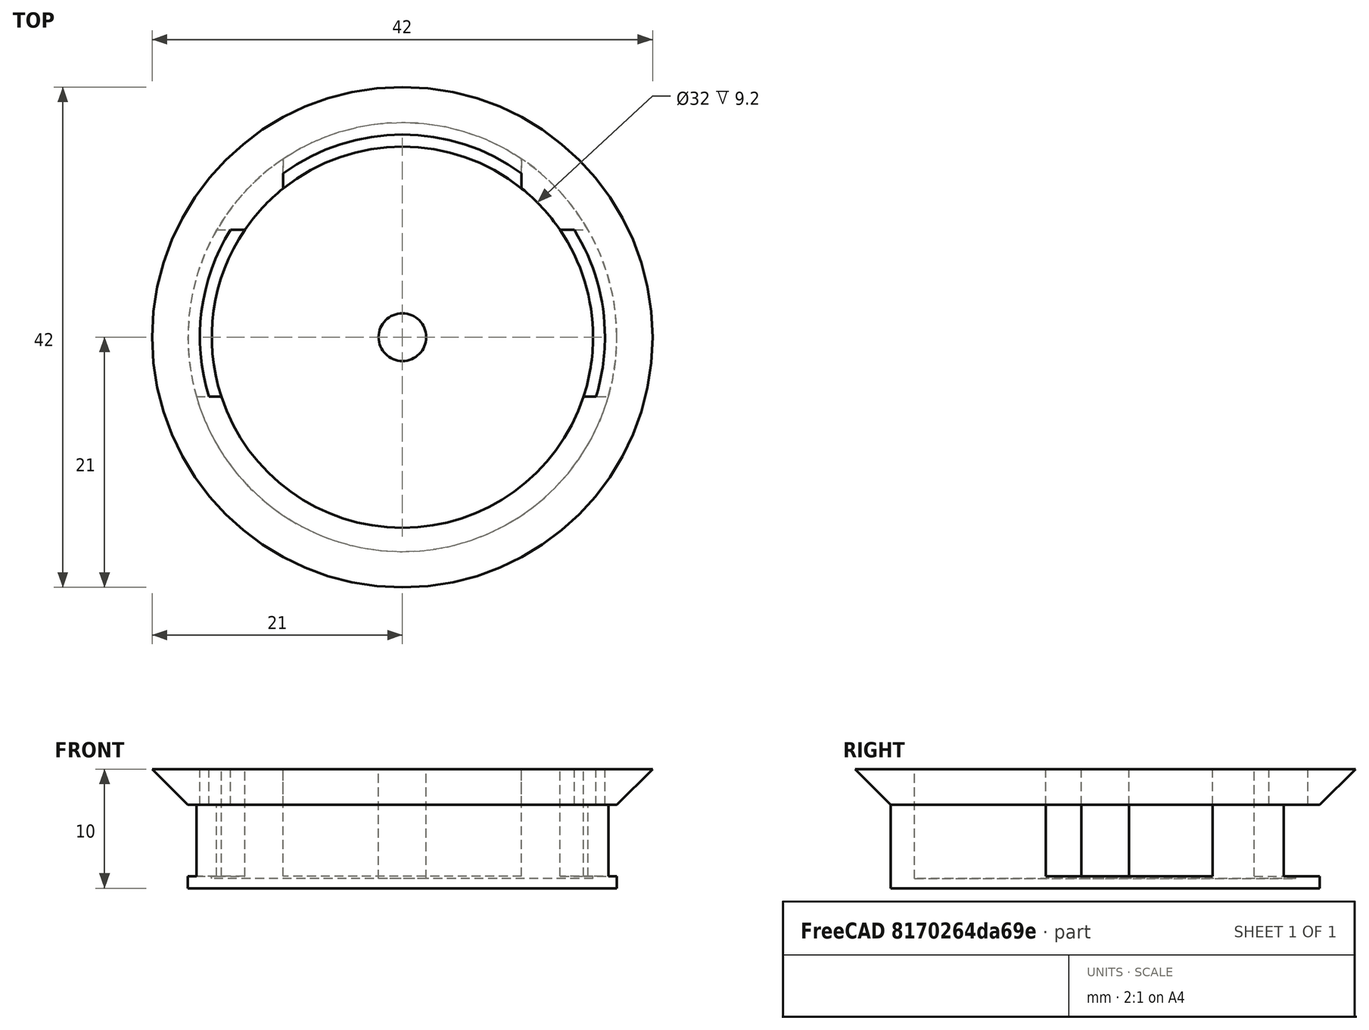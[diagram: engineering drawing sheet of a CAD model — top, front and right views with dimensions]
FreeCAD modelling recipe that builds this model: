
FCSTD DOCUMENT  (FreeCAD 0.17R13541 (Git))
Label: valve top 03
License: All rights reserved
LicenseURL: http://en.wikipedia.org/wiki/All_rights_reserved
objects: Part::Cylinder×5, Part::Cut×3, Part::MultiFuse×3, Part::Box×2, Part::Cone×1
note: 14 computed .brp shape members not serialized (recipe doc carries the construction recipe); baked Part::Feature solids carry a one-line shape summary decoded from their .brp

FEATURE [Part::Cylinder] Cylinder  label="top"
  Angle = 360
  AttacherType = Attacher::AttachEngine3D
  Height = 0.8
  Radius = 18
FEATURE [Part::Cylinder] Cylinder001  label="sides"
  Angle = 360
  AttacherType = Attacher::AttachEngine3D
  Height = 10
  Radius = 18
FEATURE [Part::Cylinder] Cylinder002  label="hole"
  Angle = 360
  AttacherType = Attacher::AttachEngine3D
  Height = 11
  Radius = 16
FEATURE [Part::Cut] Cut  label="side_wall"
  Base = -> Cylinder001
  Tool = -> Cylinder002
FEATURE [Part::Box] Box  label="Cube"
  AttacherType = Attacher::AttachEngine3D
  Height = 10
  Length = 20
  Placement = pos=(-10,8,1) rot=(0,0,1;0rad)
  Width = 14
FEATURE [Part::Box] Box001  label="Cube001"
  AttacherType = Attacher::AttachEngine3D
  Height = 10
  Length = 44
  Placement = pos=(-22,-5,1) rot=(0,0,1;0rad)
  Width = 14
FEATURE [Part::MultiFuse] Fusion  label="cuts"
  Shapes = -> [Box001,Box]
FEATURE [Part::MultiFuse] Fusion001  label="cap"
  Shapes = -> [Cut,Cylinder]
FEATURE [Part::Cut] Cut001
  Base = -> Fusion001
  Tool = -> Fusion
FEATURE [Part::Cone] Cone  label="ring"
  Angle = 360
  AttacherType = Attacher::AttachEngine3D
  Height = 3
  Placement = pos=(0,0,7) rot=(0,0,1;0rad)
  Radius1 = 18
  Radius2 = 21
FEATURE [Part::Cylinder] Cylinder003  label="hole001"
  Angle = 360
  AttacherType = Attacher::AttachEngine3D
  Height = 5
  Placement = pos=(0,0,7) rot=(0,0,1;0rad)
  Radius = 17
FEATURE [Part::Cut] Cut002
  Base = -> Cone
  Tool = -> Cylinder003
FEATURE [Part::Cylinder] Cylinder004  label="Cylinder"
  Angle = 360
  AttacherType = Attacher::AttachEngine3D
  Height = 10
  Radius = 2
FEATURE [Part::MultiFuse] Fusion002
  Shapes = -> [Cylinder004,Cut001,Cut002]
